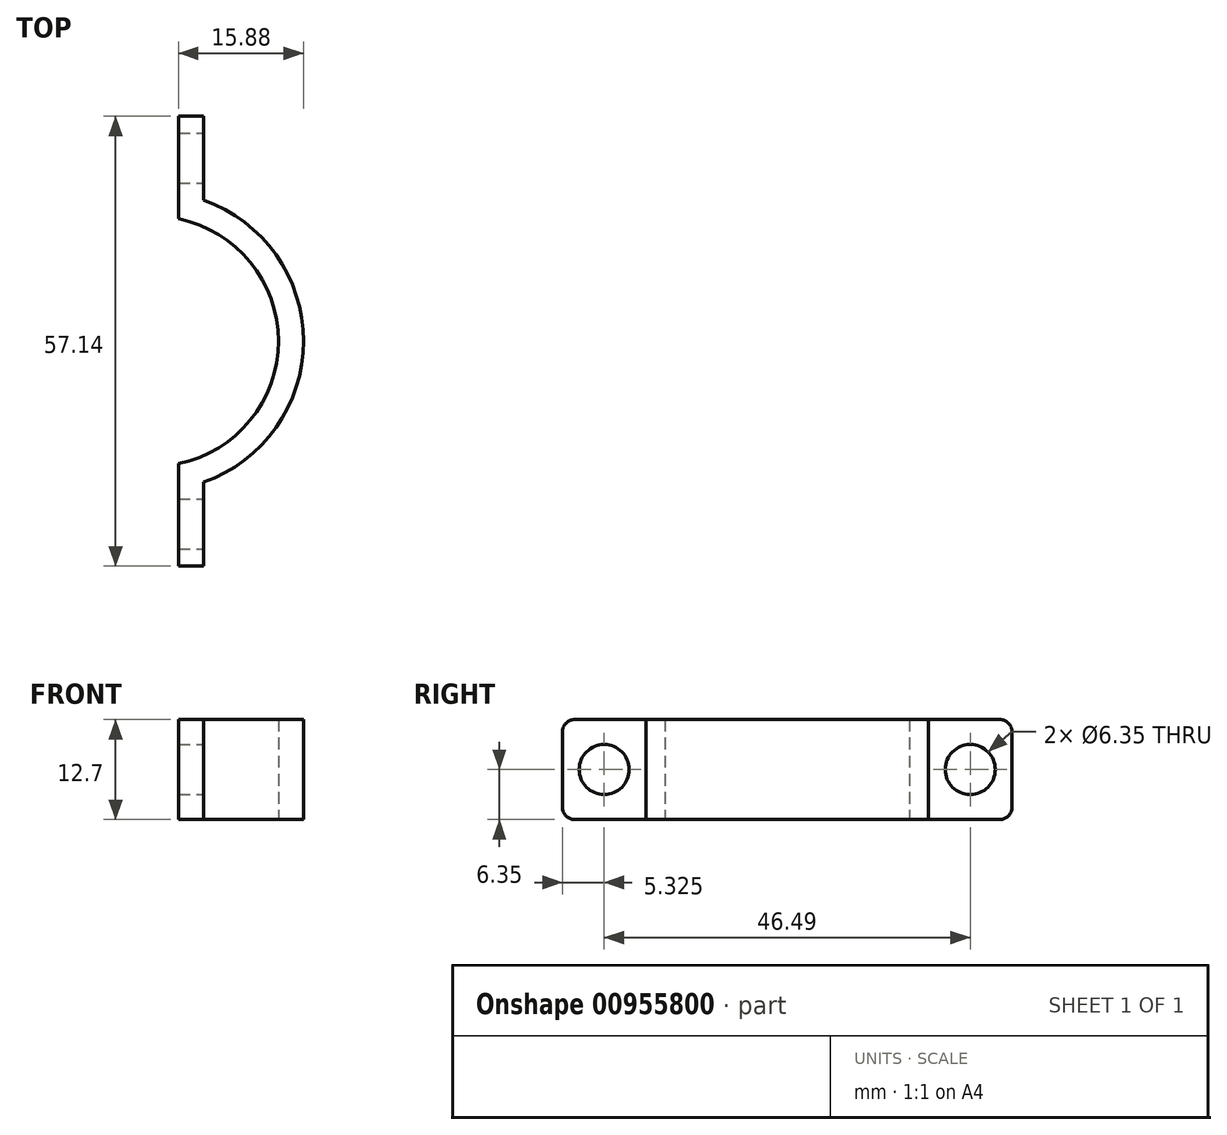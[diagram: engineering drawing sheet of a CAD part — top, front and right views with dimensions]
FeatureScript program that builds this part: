
annotation { "Feature Type Name" : "Feature", "Feature Type Description" : "" }
export const myFeature = defineFeature(function(context is Context, id is Id, definition is map)
    precondition{}
    {
        {
            var Q0;
            Q0=qCreatedBy(makeId("Top.planeOp"),FACE);
            var sketch = newSketch(context, id + "F0", { "sketchPlane" : qUnion([Q0])});
            skArc(sketch, "E0", {"start": v(0, -15.88) * mm, "mid": v(15.88, 0) * mm, "end": v(0, 15.88) * mm});
            skLineSegment(sketch, "E1", {"start": v(3.18, 15.55) * mm, "end": v(3.17, 28.58) * mm});
            skLineSegment(sketch, "E2", {"start": v(3.18, 28.58) * mm, "end": v(6.35, 28.58) * mm});
            skLineSegment(sketch, "E3.MirrorCS", {"start": v(3.18, -15.55) * mm, "end": v(3.17, -28.58) * mm});
            skLineSegment(sketch, "E4.MirrorCS", {"start": v(3.18, -28.58) * mm, "end": v(6.35, -28.58) * mm});
            skArc(sketch, "E5", {"start": v(3.17, -18.73) * mm, "mid": v(19.05, 0) * mm, "end": v(3.17, 18.73) * mm});
            skLineSegment(sketch, "E6", {"start": v(6.35, 28.58) * mm, "end": v(6.35, 17.92) * mm});
            skLineSegment(sketch, "E7", {"start": v(6.35, -28.58) * mm, "end": v(6.35, -17.92) * mm});
            skSolve(sketch);
        }
        {
            var Q0;
            {var subQ4=sQuery(id+"F0.wireOp",EDGE,"E1");var subQ5=sQuery(id+"F0.wireOp",EDGE,"E0");var subQ6=makeQuery(id+"F0.imprint","INTERSECT",VERTEX,{"derivedFrom":[subQ5,subQ4]});Q0=makeQuery(id+"F0.imprint","IMPRINT",FACE,{"disambiguationData":[TD([[makeQuery(id+"F0.imprint","IMPRINT",EDGE,{"disambiguationData":[TD([[subQ6,1.0]])],"derivedFrom":subQ5}),-1.0]])]});}
            var Q1;
            {var subQ0=sQuery(id+"F0.wireOp",EDGE,"E2");Q1=makeQuery(id+"F0.imprint","IMPRINT",FACE,{"disambiguationData":[TD([[makeQuery(id+"F0.imprint","IMPRINT",EDGE,{"derivedFrom":subQ0}),-1.0]])]});}
            var Q2;
            {var subQ0=sQuery(id+"F0.wireOp",EDGE,"E4.MirrorCS");Q2=makeQuery(id+"F0.imprint","IMPRINT",FACE,{"disambiguationData":[TD([[makeQuery(id+"F0.imprint","IMPRINT",EDGE,{"derivedFrom":subQ0}),1.0]])]});}
            extrude(context, id + "F1", {"entities" : qUnion([Q0, Q1, Q2]), "depth" : 12.7 * mm, "offsetDistance" : 25.4 * mm});
        }
        {
            var Q0;
            Q0=makeQuery(id+"F1.opExtrude","CAP_EDGE",EDGE,{"disambiguationData":[OSD([sQuery(id+"F0.wireOp",EDGE,"E2")])],"isStart":false});
            var Q1;
            Q1=makeQuery(id+"F1.opExtrude","CAP_EDGE",EDGE,{"disambiguationData":[OSD([sQuery(id+"F0.wireOp",EDGE,"E2")])],"isStart":true});
            var Q2;
            Q2=makeQuery(id+"F1.opExtrude","CAP_EDGE",EDGE,{"disambiguationData":[OSD([sQuery(id+"F0.wireOp",EDGE,"E4.MirrorCS")])],"isStart":true});
            var Q3;
            Q3=makeQuery(id+"F1.opExtrude","CAP_EDGE",EDGE,{"disambiguationData":[OSD([sQuery(id+"F0.wireOp",EDGE,"E4.MirrorCS")])],"isStart":false});
            fillet(context, id + "F2", {"entities" : qUnion([Q0, Q1, Q2, Q3]), "radius" : 1.59 * mm, "tangentPropagation" : true, "allowEdgeOverflow" : false});
        }
        {
            var Q0;
            Q0=makeQuery(id+"F1.opExtrude","SWEPT_FACE",FACE,{"disambiguationData":[OSD([sQuery(id+"F0.wireOp",EDGE,"E7")])]});
            var sketch = newSketch(context, id + "F3", { "sketchPlane" : qUnion([Q0])});
            skLineSegment(sketch, "E8", {"start": v(-28.58, 6.35) * mm, "end": v(-17.92, 6.35) * mm});
            skPoint(sketch, "E9", {"position": v(-23.25, 6.35) * mm});
            skLineSegment(sketch, "E10", {"start": v(0, 24.08) * mm, "end": v(0, -13.13) * mm});
            skPoint(sketch, "E11.MirrorP", {"position": v(23.25, 6.35) * mm});
            skSolve(sketch);
        }
        {
            var Q0;
            Q0=sQuery(id+"F3.wireOp",VERTEX,"E9");
            var Q1;
            Q1=sQuery(id+"F3.wireOp",VERTEX,"E11.MirrorP");
            var Q2;
            Q2=makeQuery(id+"F1.opExtrude","SWEPT_BODY",BODY,{"disambiguationData":[OSD([sQuery(id+"F0.wireOp",EDGE,"E0"),sQuery(id+"F0.wireOp",EDGE,"E1"),sQuery(id+"F0.wireOp",EDGE,"E2"),sQuery(id+"F0.wireOp",EDGE,"E4.MirrorCS"),sQuery(id+"F0.wireOp",EDGE,"E3.MirrorCS"),sQuery(id+"F0.wireOp",EDGE,"E5"),sQuery(id+"F0.wireOp",EDGE,"E6"),sQuery(id+"F0.wireOp",EDGE,"E7")])]});
            hole(context, id + "F4", {"style" : HoleStyle.SIMPLE, "endStyle" : HoleEndStyle.THROUGH, "holeDiameter" : 6.35 * mm, "majorDiameter" : 6.35 * mm, "isTappedThrough" : true, "tappedDepth" : 12.7 * mm, "tapClearance" : 3, "locations" : qUnion([Q0, Q1]), "scope" : qUnion([Q2])});
        }
    });
